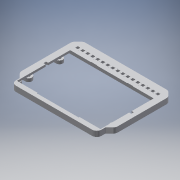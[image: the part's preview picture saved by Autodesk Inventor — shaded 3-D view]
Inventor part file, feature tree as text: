
AUTODESK INVENTOR PART (.ipt)
format: ipt  version: 2017 SP1 (Build 210196100, 196)  size: 1,082,880 bytes
history: native  units: mm
features: reference x44, projected_geometry x18, plane x9, extrude x8, sketch x6, other x5, shell x2
ambient origin geometry x8: Origin, YZ Plane, XZ Plane, XY Plane, X Axis, Y Axis, Z Axis, Center Point
bodies: Volumenkörper1 (feature_tree), Volumenkörper2 (feature_tree), Volumenkörper3 (feature_tree)
feature tree (92):
  plane  "Arbeitsebene1"
  sketch  "Skizze1"  dims[d0=10.0mm d1=0.0mm d4=10.0mm d5=0.0mm]
  plane  "Arbeitsebene2"
  extrude  "Extrusion1"  Depth=10.0mm TaperAngle=0.0deg
  plane  "Arbeitsebene3"
  plane  "Arbeitsebene4"
  plane  "Arbeitsebene5"
  extrude  "Extrusion2"  Depth=10.0mm TaperAngle=0.0deg
  shell  "Wandung3"  Thickness=0.5mm
  sketch  "Skizze4"  dims[d8=2.5mm d9=10.0mm d10=0.0mm d11=0.5mm]
  plane  "Arbeitsebene6"
  extrude  "Extrusion3"  Depth=6.0mm
  shell  "Wandung4"  Thickness=4.0mm
  other  "Kombinieren1"
  plane  "Arbeitsebene7"
  sketch  "Skizze7"  dims[d19=6.0mm d20=6.0mm d23=4.0mm]
  plane  "Arbeitsebene8"
  plane  "Arbeitsebene9"
  extrude  "Extrusion5"  TaperAngle=90.0deg  [1 undecoded]
  extrude  "Extrusion16"  Depth=10.0mm TaperAngle=0.0deg
  extrude  "Extrusion17"  Depth=2.5mm TaperAngle=0.0deg
  extrude  "Extrusion18"  Depth=1.0mm
  extrude  "Extrusion19"  Depth=1.0mm
  reference  "Referenz1"
  reference  "Referenz2"
  reference  "Referenz3"
  reference  "Referenz4"
  reference  "Referenz5"
  reference  "Referenz6"
  reference  "Referenz7"
  reference  "Referenz8"
  reference  "Referenz9"
  reference  "Referenz10"
  reference  "Referenz11"
  reference  "Referenz12"
  reference  "Referenz13"
  reference  "Referenz14"
  reference  "Referenz15"
  reference  "Referenz16"
  reference  "Referenz17"
  reference  "Referenz18"
  projected_geometry  "Projizierte Kontur1"
  reference  "Referenz28"
  reference  "Referenz29"
  reference  "Referenz30"
  projected_geometry  "Projizierte Kontur3"
  reference  "Referenz31"
  reference  "Referenz32"
  sketch  "Skizze23"  dims[d25=4.0mm d26=90.0deg]
  sketch  "Skizze24"  dims[d27=180.0deg d28=10.0mm d29=0.0mm]
  sketch  "Skizze25"  dims[d188=2.5mm d189=0.0mm d190=2.5mm d191=0.0mm d196=1.0mm d197=1.0mm d198=1.0mm d199=1.0mm d200=2.5mm d201=0.0mm d202=3.05mm d203=3.05mm d204=0.2mm d205=3.05mm d206=3.05mm d207=0.2mm d208=3.05mm d209=3.05mm d210=0.2mm d211=3.05mm d212=3.05mm d213=0.2mm d214=3.05mm d215=3.05mm d216=0.2mm d217=3.05mm d218=3.05mm d219=0.2mm d220=3.05mm d221=3.05mm d222=0.2mm d223=3.05mm d224=3.05mm d225=0.2mm d226=3.05mm d227=3.05mm d228=0.2mm d229=3.05mm d230=3.05mm d231=0.2mm d232=3.05mm d233=3.05mm d234=0.2mm d235=3.05mm d236=3.05mm d237=0.2mm d238=3.05mm d239=3.05mm d240=0.2mm d241=3.05mm d242=3.05mm d243=0.2mm d244=3.05mm d245=3.05mm d246=0.2mm d247=3.05mm d248=3.05mm d249=0.2mm d250=3.05mm d251=3.05mm d252=0.2mm d253=3.05mm d254=3.05mm d255=0.2mm d256=3.05mm d257=3.05mm d258=0.2mm d259=2.5mm d260=0.0mm]
  projected_geometry  "Projizierte Kontur11"
  reference  "Referenz59"
  projected_geometry  "Projizierte Kontur12"
  projected_geometry  "Projizierte Kontur13"
  projected_geometry  "Projizierte Kontur14"
  projected_geometry  "Projizierte Kontur15"
  projected_geometry  "Projizierte Kontur16"
  projected_geometry  "Projizierte Kontur17"
  projected_geometry  "Projizierte Kontur18"
  projected_geometry  "Projizierte Kontur19"
  projected_geometry  "Projizierte Kontur20"
  projected_geometry  "Projizierte Kontur21"
  projected_geometry  "Projizierte Kontur22"
  projected_geometry  "Projizierte Kontur23"
  projected_geometry  "Projizierte Kontur24"
  projected_geometry  "Projizierte Kontur25"
  projected_geometry  "Projizierte Kontur26"
  reference  "Referenz60"
  reference  "Referenz61"
  reference  "Referenz62"
  reference  "Referenz63"
  reference  "Referenz64"
  reference  "Referenz65"
  reference  "Referenz66"
  reference  "Referenz67"
  reference  "Referenz68"
  reference  "Referenz69"
  reference  "Referenz70"
  reference  "Referenz71"
  reference  "Referenz72"
  reference  "Referenz73"
  reference  "Referenz74"
  reference  "Referenz75"
  reference  "Referenz76"
  reference  "Referenz77"
  reference  "Referenz78"
  reference  "Referenz79"
  other  "<userpath>\Dropbox\Elektronik\aXe_Dashboard240XL\Gehäuse\Gehäuse.iam"
  other  "Gehäuse.iam"
  other  "PCB_SingleLedRow:1"
  other  "Schnittkanten projizieren3"
note: 1 required parameter value undecoded (feature->parameter linkage not recoverable at this tier; creation-order binding heuristic only, values carry confidence <= 0.55)
